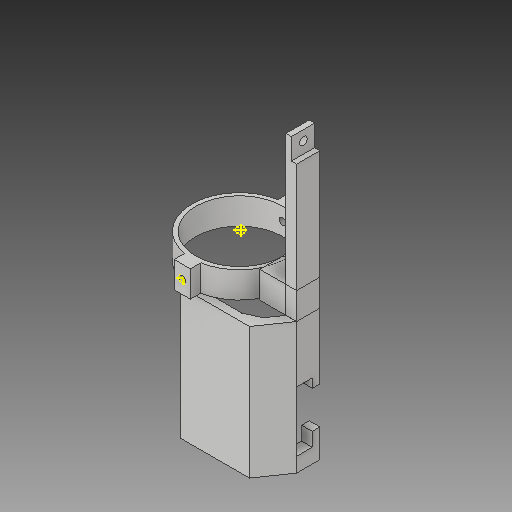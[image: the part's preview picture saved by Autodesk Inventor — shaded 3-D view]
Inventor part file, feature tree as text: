
AUTODESK INVENTOR PART (.ipt)
format: ipt  version: 2017 (Build 210142000, 142)  size: 227,328 bytes
history: native  units: mm
features: sketch x9, extrude x7, hole x4, other x3
ambient origin geometry x8: Origin, YZ Plane, XZ Plane, XY Plane, X Axis, Y Axis, Z Axis, Center Point
bodies: Solid1 (feature_tree), Solid2 (feature_tree)
feature tree (23):
  extrude  "Extrusion1"  Depth=36.0mm
  extrude  "Extrusion2"  Depth=4.0mm
  other  "Work Point1"
  other  "Work Point2"
  hole  "Hole1"  [1 undecoded]
  hole  "Hole2"  [1 undecoded]
  extrude  "Extrusion4"  Depth=60.0mm TaperAngle=0.0deg
  extrude  "Extrusion5"  Depth=2.0mm TaperAngle=0.0deg
  extrude  "Extrusion6"  Depth=14.0mm TaperAngle=0.0deg
  hole  "Hole3"  [1 undecoded]
  extrude  "Extrusion7"  Depth=2.0mm
  extrude  "Extrusion8"  Depth=2.0mm
  hole  "Hole4"  [1 undecoded]
  other  "Work Point3"
  sketch  "Sketch1"  dims[d0=33.0mm d1=36.0mm]
  sketch  "Sketch2"  dims[d2=4.0mm d4=4.0mm]
  sketch  "Sketch3"  dims[d5=4.0mm d7=10.0mm d8=0.0mm]
  sketch  "Sketch7"  dims[d10=10.0mm d11=0.0mm]
  sketch  "Sketch8"  dims[d12=10.0mm d13=10.0mm d14=2.621mm d15=6.0mm d16=4.0mm d17=2.0mm d18=90.0deg d19=43.4621mm d20=20.594885mm]
  sketch  "Sketch9"  dims[d23=33.0mm d24=6.0mm d25=4.0mm d26=2.0mm d27=90.0deg d28=8.0mm d29=20.594885mm d32=50.0mm d33=0.0mm]
  sketch  "Sketch18"  dims[d34=50.0mm d35=0.0mm d36=60.0mm d37=0.0mm]
  sketch  "Sketch19"  dims[d38=10.0mm d39=10.0mm]
  sketch  "Sketch21"  dims[d40=3.0mm d41=6.0mm d42=4.0mm d43=2.0mm d44=90.0deg d45=8.0mm d46=20.594885mm d47=2.0mm d48=0.0mm d49=14.0mm d50=0.0mm d51=33.0mm d52=33.0mm d53=33.0mm d54=6.0mm d55=4.0mm d56=2.0mm d57=90.0deg d58=8.0mm d59=20.594885mm d60=33.0mm]
note: 4 required parameter values undecoded (feature->parameter linkage not recoverable at this tier; creation-order binding heuristic only, values carry confidence <= 0.55)
